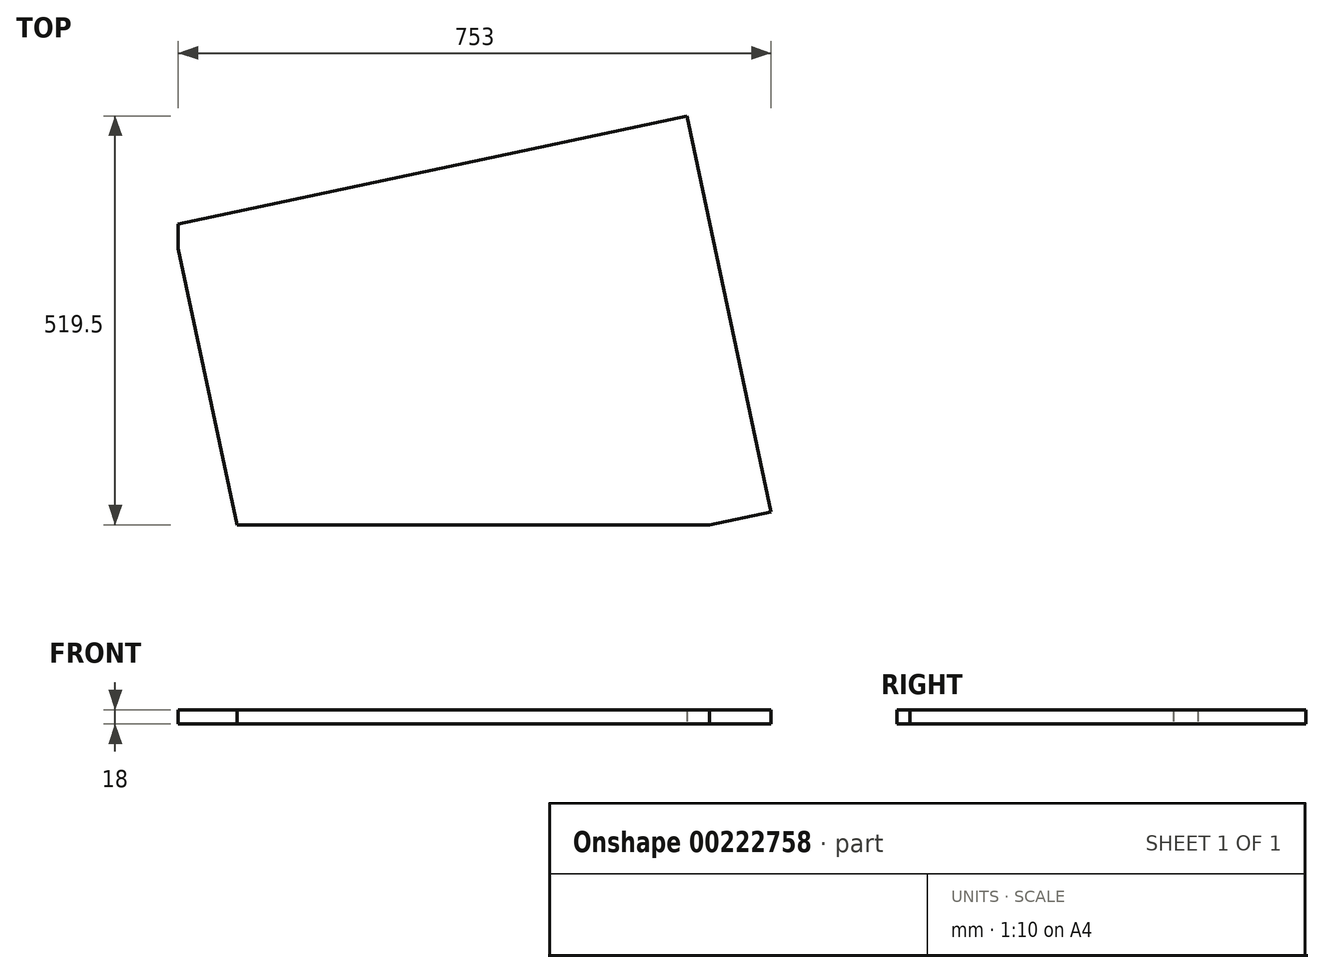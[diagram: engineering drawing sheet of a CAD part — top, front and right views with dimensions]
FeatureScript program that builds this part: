
annotation { "Feature Type Name" : "Feature", "Feature Type Description" : "" }
export const myFeature = defineFeature(function(context is Context, id is Id, definition is map)
    precondition{}
    {
        {
            var Q0;
            Q0=qCreatedBy(makeId("Top.planeOp"),FACE);
            var sketch = newSketch(context, id + "F0", { "sketchPlane" : qUnion([Q0])});
            skLineSegment(sketch, "E0", {"start": v(-399.58, -63.64) * mm, "end": v(-1052.21, -202.36) * mm, "construction": true});
            skLineSegment(sketch, "E1", {"start": v(-977.57, -552.5) * mm, "end": v(-977.57, -552.5) * mm});
            skLineSegment(sketch, "E2", {"start": v(-977.57, -552.5) * mm, "end": v(-377.57, -552.5) * mm, "construction": true});
            skLineSegment(sketch, "E3", {"start": v(-977.57, -186.5) * mm, "end": v(-377.57, -186.5) * mm, "construction": true});
            skLineSegment(sketch, "E4", {"start": v(-377.57, -186.5) * mm, "end": v(-377.57, -552.5) * mm, "construction": true});
            skLineSegment(sketch, "E5", {"start": v(-289.21, -552.5) * mm, "end": v(-289.21, -552.5) * mm});
            skLineSegment(sketch, "E6", {"start": v(-289.21, -552.5) * mm, "end": v(-289.21, 21.5) * mm, "construction": true});
            skLineSegment(sketch, "E7", {"start": v(-289.21, 21.5) * mm, "end": v(-1052.21, 21.5) * mm, "construction": true});
            skLineSegment(sketch, "E8", {"start": v(-1052.21, -202.36) * mm, "end": v(-1052.21, -201.35) * mm});
            skLineSegment(sketch, "E9", {"start": v(-977.57, -552.5) * mm, "end": v(-1052.21, -201.35) * mm});
            skLineSegment(sketch, "E10", {"start": v(-977.57, -552.5) * mm, "end": v(-377.57, -552.5) * mm});
            skLineSegment(sketch, "E11", {"start": v(-377.57, -552.5) * mm, "end": v(-299.21, -535.84) * mm});
            skLineSegment(sketch, "E12", {"start": v(-299.21, -535.84) * mm, "end": v(-406.1, -33) * mm});
            skLineSegment(sketch, "E13", {"start": v(-299.21, -535.84) * mm, "end": v(-289.21, -535.84) * mm, "construction": true});
            skLineSegment(sketch, "E14", {"start": v(-1052.21, -202.36) * mm, "end": v(-1052.21, 21.5) * mm, "construction": true});
            skLineSegment(sketch, "E15", {"start": v(-377.57, -552.5) * mm, "end": v(-289.21, -552.5) * mm, "construction": true});
            skLineSegment(sketch, "E16", {"start": v(-1052.21, -201.35) * mm, "end": v(-1052.21, -552.5) * mm, "construction": true});
            skLineSegment(sketch, "E17", {"start": v(-1052.21, -552.5) * mm, "end": v(-977.57, -552.5) * mm, "construction": true});
            skLineSegment(sketch, "E18", {"start": v(-977.57, -552.5) * mm, "end": v(-977.57, -186.5) * mm, "construction": true});
            skLineSegment(sketch, "E19", {"start": v(-1052, -202.32) * mm, "end": v(-1052.21, -202.36) * mm, "construction": true});
            skLineSegment(sketch, "E20", {"start": v(-1052.21, -201.35) * mm, "end": v(-1052, -202.32) * mm, "construction": true});
            skLineSegment(sketch, "E21", {"start": v(-377.57, -186.5) * mm, "end": v(-373.65, -185.66) * mm, "construction": true});
            skLineSegment(sketch, "E22", {"start": v(-1058.52, -171.68) * mm, "end": v(-1052.21, -170.34) * mm});
            skLineSegment(sketch, "E23", {"start": v(-1052.21, -202.36) * mm, "end": v(-1052.21, -170.34) * mm});
            skLineSegment(sketch, "E24", {"start": v(-1101.55, -578.85) * mm, "end": v(-977.57, -552.5) * mm, "construction": true});
            skLineSegment(sketch, "E25", {"start": v(-1058.52, -171.68) * mm, "end": v(-406.1, -33) * mm});
            skLineSegment(sketch, "E26", {"start": v(-406.1, -33) * mm, "end": v(-289.21, -8.16) * mm, "construction": true});
            skLineSegment(sketch, "E27", {"start": v(-406.1, -33) * mm, "end": v(-289.21, -33) * mm, "construction": true});
            skLineSegment(sketch, "E28", {"start": v(-299.21, -535.84) * mm, "end": v(-295.67, -552.5) * mm, "construction": true});
            skPoint(sketch, "E29", {"position": v(-295.67, -552.5) * mm});
            skLineSegment(sketch, "E30", {"start": v(-299.21, -535.84) * mm, "end": v(-289.21, -533.72) * mm, "construction": true});
            skSolve(sketch);
        }
        {
            var Q0;
            {var subQ0=sQuery(id+"F0.wireOp",EDGE,"E10");Q0=makeQuery(id+"F0.imprint","IMPRINT",FACE,{"disambiguationData":[TD([[makeQuery(id+"F0.imprint","IMPRINT",EDGE,{"derivedFrom":subQ0}),1.0]])]});}
            extrude(context, id + "F1", {"entities" : qUnion([Q0]), "depth" : 18 * mm});
        }
    });
